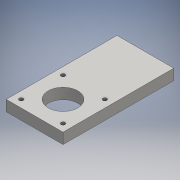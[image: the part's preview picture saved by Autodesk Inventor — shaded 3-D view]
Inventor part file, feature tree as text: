
AUTODESK INVENTOR PART (.ipt)
format: ipt  version: 2016 SP1 (Build 200210100, 210)  size: 104,448 bytes
history: native  units: mm
features: extrude x2, sketch x2, projected_geometry x1
ambient origin geometry x8: Origin, YZ Plane, XZ Plane, XY Plane, X Axis, Y Axis, Z Axis, Center Point
bodies: Solid1 (feature_tree)
feature tree (5):
  extrude  "Extrusion1"  Depth=8.0mm TaperAngle=0.0deg
  extrude  "Extrusion2"  [1 undecoded]
  sketch  "Sketch1"  dims[d0=8.0mm d1=0.0mm d2=40.0mm d3=0.0mm]
  sketch  "Sketch2"
  projected_geometry  "Projected Loop1"
note: 1 required parameter value undecoded (feature->parameter linkage not recoverable at this tier; creation-order binding heuristic only, values carry confidence <= 0.55)
